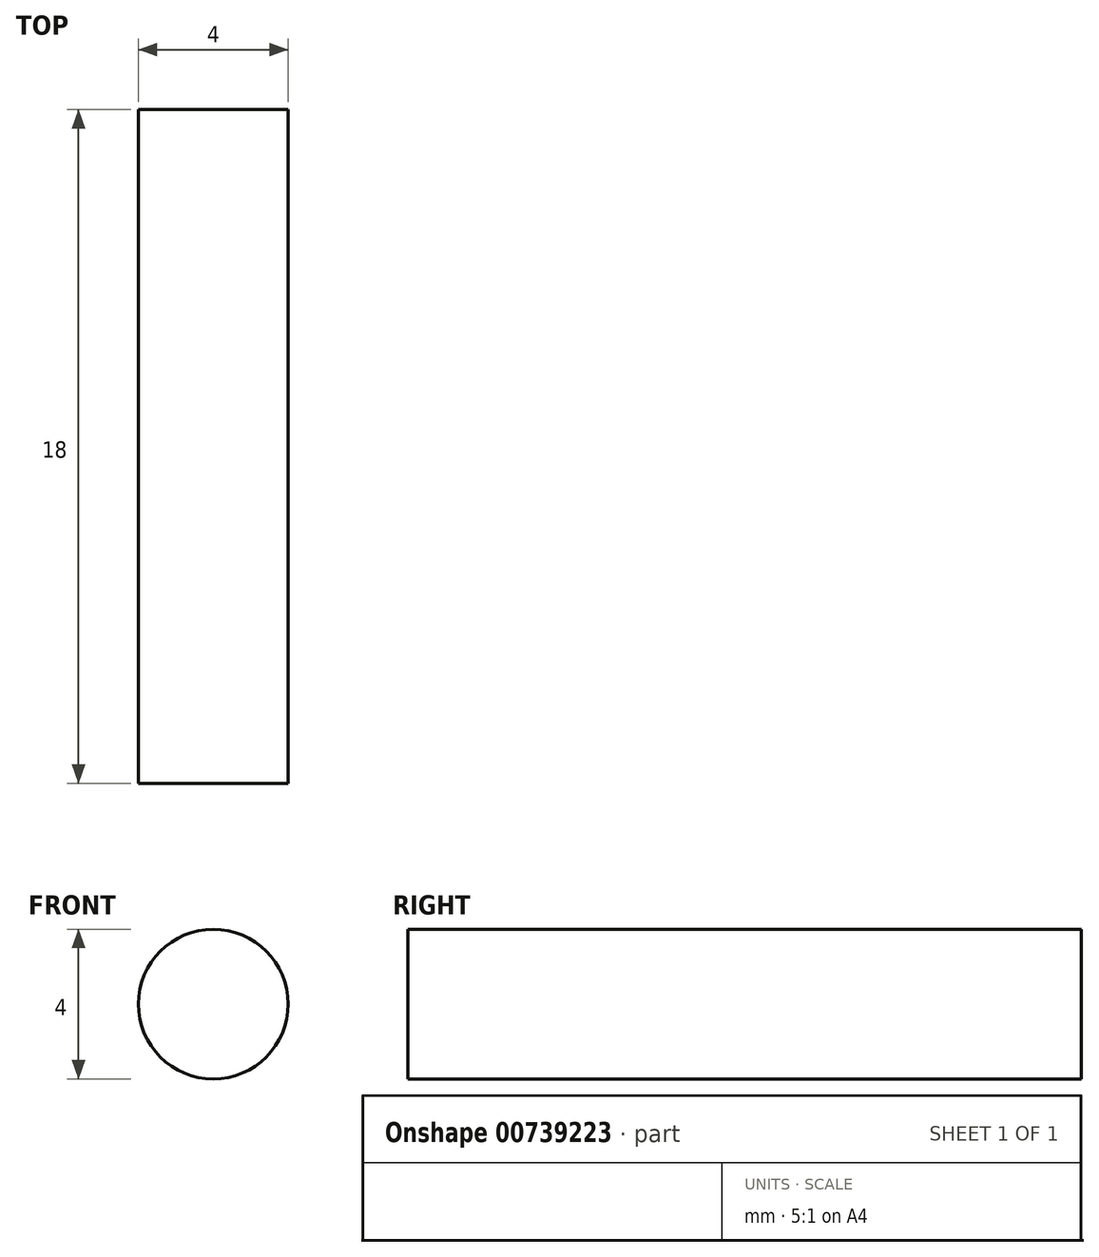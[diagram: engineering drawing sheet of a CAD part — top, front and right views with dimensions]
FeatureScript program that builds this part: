
annotation { "Feature Type Name" : "Feature", "Feature Type Description" : "" }
export const myFeature = defineFeature(function(context is Context, id is Id, definition is map)
    precondition{}
    {
        {
            var Q0;
            Q0=qCreatedBy(makeId("Front.planeOp"),FACE);
            var sketch = newSketch(context, id + "F0", { "sketchPlane" : qUnion([Q0])});
            skCircle(sketch, "E0", {"center": v(-14.89, 7.07) * mm, "radius": 2 * mm});
            skSolve(sketch);
        }
        {
            var Q0;
            Q0 = qSketchRegion(id + "F0", true);
            extrude(context, id + "F1", {"entities" : qUnion([Q0]), "depth" : 18 * mm, "offsetDistance" : 25.4 * mm});
        }
    });
